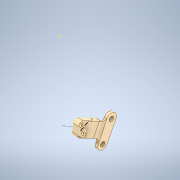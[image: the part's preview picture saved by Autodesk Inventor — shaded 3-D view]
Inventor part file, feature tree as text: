
AUTODESK INVENTOR PART (.ipt)
format: ipt  version: 2020 (Build 240168000, 168)  size: 274,944 bytes
history: native  units: in
note: dims shown in document units (in); Inventor stores cm internally (conversion verified against a paired STEP export)
features: sketch x8, fillet x5, extrude x4, projected_geometry x1
ambient origin geometry x8: Origin, YZ Plane, XZ Plane, XY Plane, X Axis, Y Axis, Z Axis, Center Point
bodies: Body1 (feature_tree)
feature tree (18):
  sketch  "Sketch3"  dims[d0=0.0039in d1=0.2362in d2=0.0in]
  sketch  "Sketch4"  dims[d3=0.315in d4=0.1575in d5=0.315in d6=0.0787in d7=0.0in d8=0.1181in]
  extrude  "Extrusion1"  Depth=0.2362in TaperAngle=0.0deg
  extrude  "Extrusion2"  Depth=0.1575in
  fillet  "Fillet1"  Radius=0.315in
  sketch  "Sketch7"  dims[d16=0.2008in]
  fillet  "Fillet2"  Radius=0.0787in
  fillet  "Fillet3"  Radius=0.1181in
  extrude  "Extrusion3"  Depth=0.1181in
  extrude  "Extrusion4"  Depth=0.0787in
  fillet  "Fillet4"  Radius=0.0787in
  fillet  "Fillet5"  Radius=0.0787in
  sketch  "Sketch9"  dims[d18=0.1181in d19=0.0in]
  sketch  "Sketch10"  dims[d20=0.1969in d21=0.1969in d22=0.3717in d23=0.0787in]
  sketch  "Sketch5"  dims[d9=0.1102in d10=0.1181in]
  sketch  "Sketch6"  dims[d11=0.2047in d12=0.0787in d13=0.0787in d14=0.0787in d15=0.0in]
  sketch  "Sketch8"  dims[d17=0.2008in]
  projected_geometry  "Projected Loop2"
